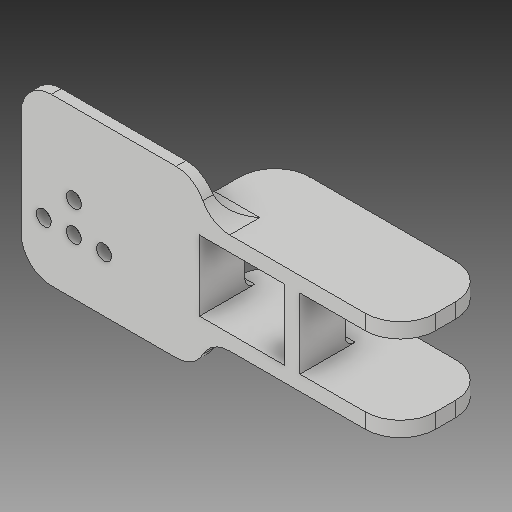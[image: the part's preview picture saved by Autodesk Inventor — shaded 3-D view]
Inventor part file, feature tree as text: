
AUTODESK INVENTOR PART (.ipt)
format: ipt  version: 2019 (Build 230136000, 136)  size: 265,728 bytes
history: native  units: mm
features: sketch x7, projected_geometry x7, extrude x6, fillet x4, hole x1
ambient origin geometry x8: Origin, YZ Plane, XZ Plane, XY Plane, X Axis, Y Axis, Z Axis, Center Point
bodies: Solid1 (feature_tree)
feature tree (25):
  extrude  "Extrusion1"  Depth=3.0mm
  hole  "Hole1"  [1 undecoded]
  extrude  "Extrusion6"  Depth=6.0mm
  extrude  "Extrusion7"  Depth=6.0mm
  extrude  "Extrusion8"  Depth=6.0mm
  fillet  "Fillet18"  Radius=6.0mm
  extrude  "Extrusion10"  Depth=6.0mm
  fillet  "Fillet23"  Radius=16.5mm
  fillet  "Fillet24"  Radius=3.0mm
  extrude  "Extrusion11"  Depth=3.0mm
  fillet  "Fillet25"  Radius=7.0mm
  sketch  "Sketch1"  dims[d0=2.0mm d1=3.0mm]
  sketch  "Sketch2"  dims[d2=42.0mm d3=18.0mm]
  projected_geometry  "Projected Loop1"
  sketch  "Sketch9"  dims[d4=33.0mm d5=0.0mm d7=6.0mm]
  projected_geometry  "Projected Loop7"
  sketch  "Sketch10"  dims[d8=6.0mm d9=6.0mm]
  projected_geometry  "Projected Loop8"
  projected_geometry  "Projected Loop9"
  sketch  "Sketch11"  dims[d11=11.0mm d12=6.0mm d14=6.0mm]
  projected_geometry  "Projected Loop10"
  sketch  "Sketch15"  dims[d15=6.0mm]
  projected_geometry  "Projected Loop14"
  sketch  "Sketch16"  dims[d16=3.0mm d17=6.0mm d18=4.0mm d19=2.0mm d20=90.0deg d21=8.0mm d22=20.594885mm d69=11.0mm d81=16.5mm d82=3.0mm d83=3.0mm d84=7.0mm d85=7.0mm d86=40.0mm d87=0.0mm d88=45.0mm d89=0.0mm d92=3.0mm d95=45.0mm d96=0.0mm d97=20.0mm d98=7.0mm d105=9.0mm d106=45.0mm d107=0.0mm d108=2.0mm d109=4.0mm d110=3.0mm d111=10.0mm d112=0.0mm d113=6.0mm]
  projected_geometry  "Projected Loop15"
note: 1 required parameter value undecoded (feature->parameter linkage not recoverable at this tier; creation-order binding heuristic only, values carry confidence <= 0.55)
